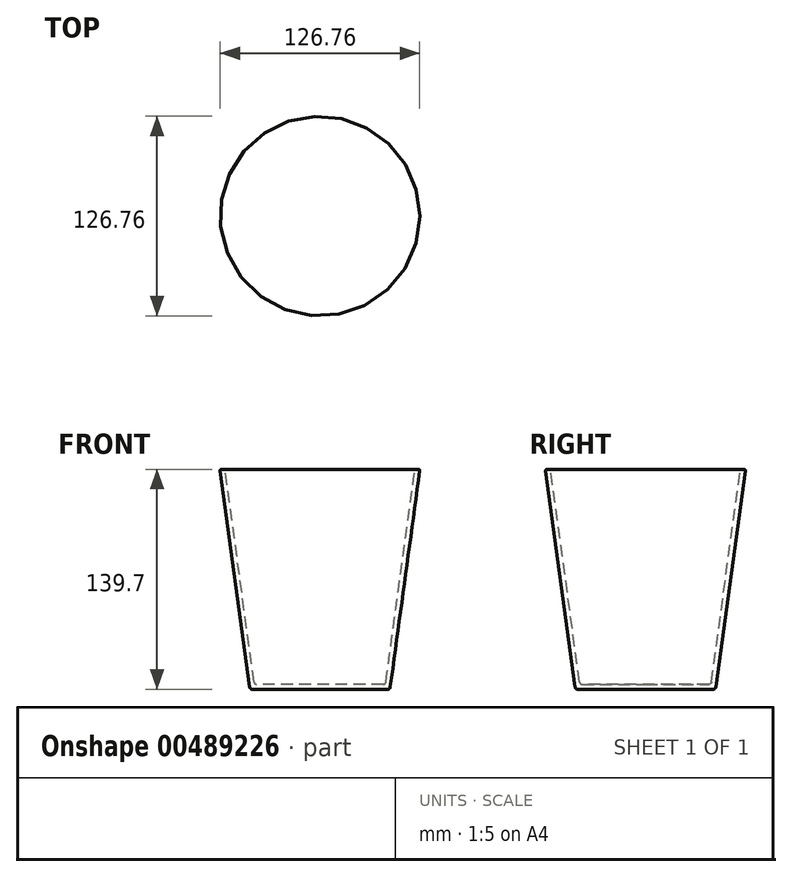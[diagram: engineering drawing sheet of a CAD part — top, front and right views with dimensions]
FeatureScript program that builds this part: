
annotation { "Feature Type Name" : "Feature", "Feature Type Description" : "" }
export const myFeature = defineFeature(function(context is Context, id is Id, definition is map)
    precondition{}
    {
        {
            var Q0;
            Q0=qCreatedBy(makeId("Front.planeOp"),FACE);
            var sketch = newSketch(context, id + "F0", { "sketchPlane" : qUnion([Q0])});
            skLineSegment(sketch, "E0", {"start": v(0, 0) * mm, "end": v(43.06, 0) * mm});
            skLineSegment(sketch, "E1", {"start": v(44.64, 1.37) * mm, "end": v(63.38, 138.8) * mm});
            skLineSegment(sketch, "E2", {"start": v(60.2, 139.01) * mm, "end": v(41.87, 4.55) * mm});
            skLineSegment(sketch, "E3", {"start": v(40.3, 3.17) * mm, "end": v(0, 3.17) * mm});
            skLineSegment(sketch, "E4", {"start": v(0, 3.18) * mm, "end": v(0, 0) * mm});
            skLineSegment(sketch, "E5", {"start": v(62.6, 139.7) * mm, "end": v(60.99, 139.7) * mm});
            skPoint(sketch, "E6.visualSharp", {"position": v(41.68, 3.18) * mm});
            skArc(sketch, "E6.filletArc", {"start": v(40.3, 3.18) * mm, "mid": v(41.34, 3.57) * mm, "end": v(41.87, 4.55) * mm});
            skPoint(sketch, "E7.visualSharp", {"position": v(44.45, 0) * mm});
            skArc(sketch, "E7.filletArc", {"start": v(43.06, 0) * mm, "mid": v(44.1, 0.4) * mm, "end": v(44.64, 1.37) * mm});
            skPoint(sketch, "E8.visualSharp", {"position": v(60.3, 139.7) * mm});
            skArc(sketch, "E8.filletArc", {"start": v(60.99, 139.7) * mm, "mid": v(60.47, 139.5) * mm, "end": v(60.2, 139.01) * mm});
            skPoint(sketch, "E9.visualSharp", {"position": v(63.5, 139.7) * mm});
            skArc(sketch, "E9.filletArc", {"start": v(63.38, 138.8) * mm, "mid": v(63.19, 139.43) * mm, "end": v(62.6, 139.7) * mm});
            skSolve(sketch);
        }
        {
            var Q0;
            Q0=makeQuery(id+"F0.imprint","IMPRINT",FACE,{"disambiguationData":[TD([[makeQuery(id+"F0.imprint","IMPRINT",EDGE,{"derivedFrom":sQuery(id+"F0.wireOp",EDGE,"E0")}),1.0]])]});
            var Q1;
            Q1=sQuery(id+"F0.wireOp",EDGE,"E4");
            revolve(context, id + "F1", {"entities" : qUnion([Q0]), "axis" : qUnion([Q1]), "revolveType" : RevolveType.FULL});
        }
    });
